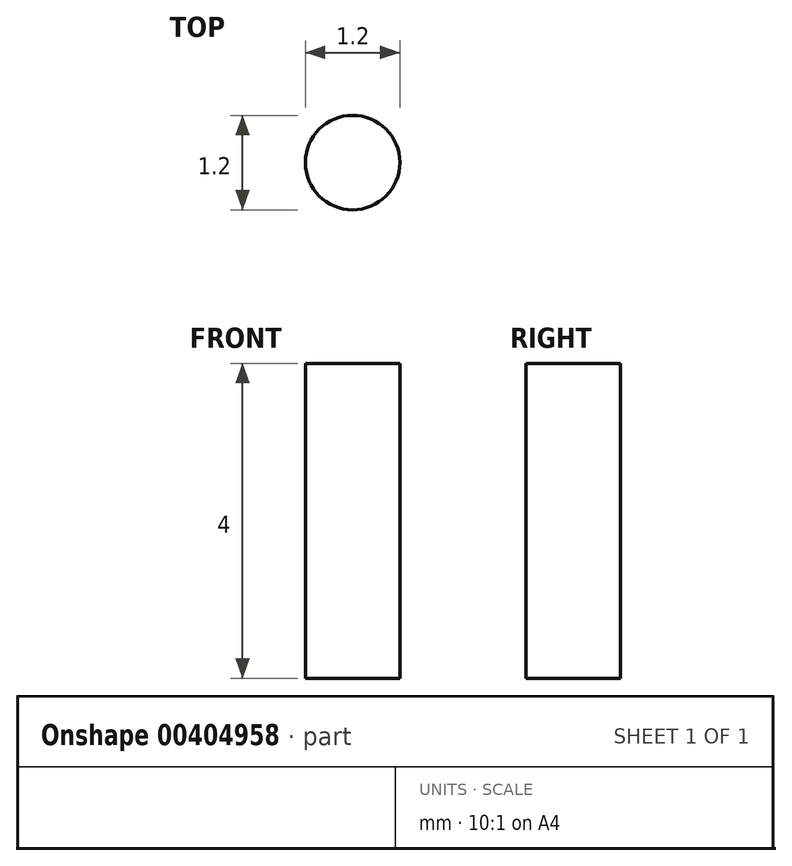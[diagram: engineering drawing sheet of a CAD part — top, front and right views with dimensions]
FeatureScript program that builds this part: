
annotation { "Feature Type Name" : "Feature", "Feature Type Description" : "" }
export const myFeature = defineFeature(function(context is Context, id is Id, definition is map)
    precondition{}
    {
        {
            var Q0;
            Q0=qCreatedBy(makeId("Top.planeOp"),FACE);
            var sketch = newSketch(context, id + "F0", { "sketchPlane" : qUnion([Q0])});
            skCircle(sketch, "E0", {"center": v(0, 0) * mm, "radius": 0.6 * mm});
            skSolve(sketch);
        }
        {
            var Q0;
            Q0=qSketchRegion(id+"F0",true);
            extrude(context, id + "F1", {"entities" : qUnion([Q0]), "depth" : 4 * mm});
        }
    });
